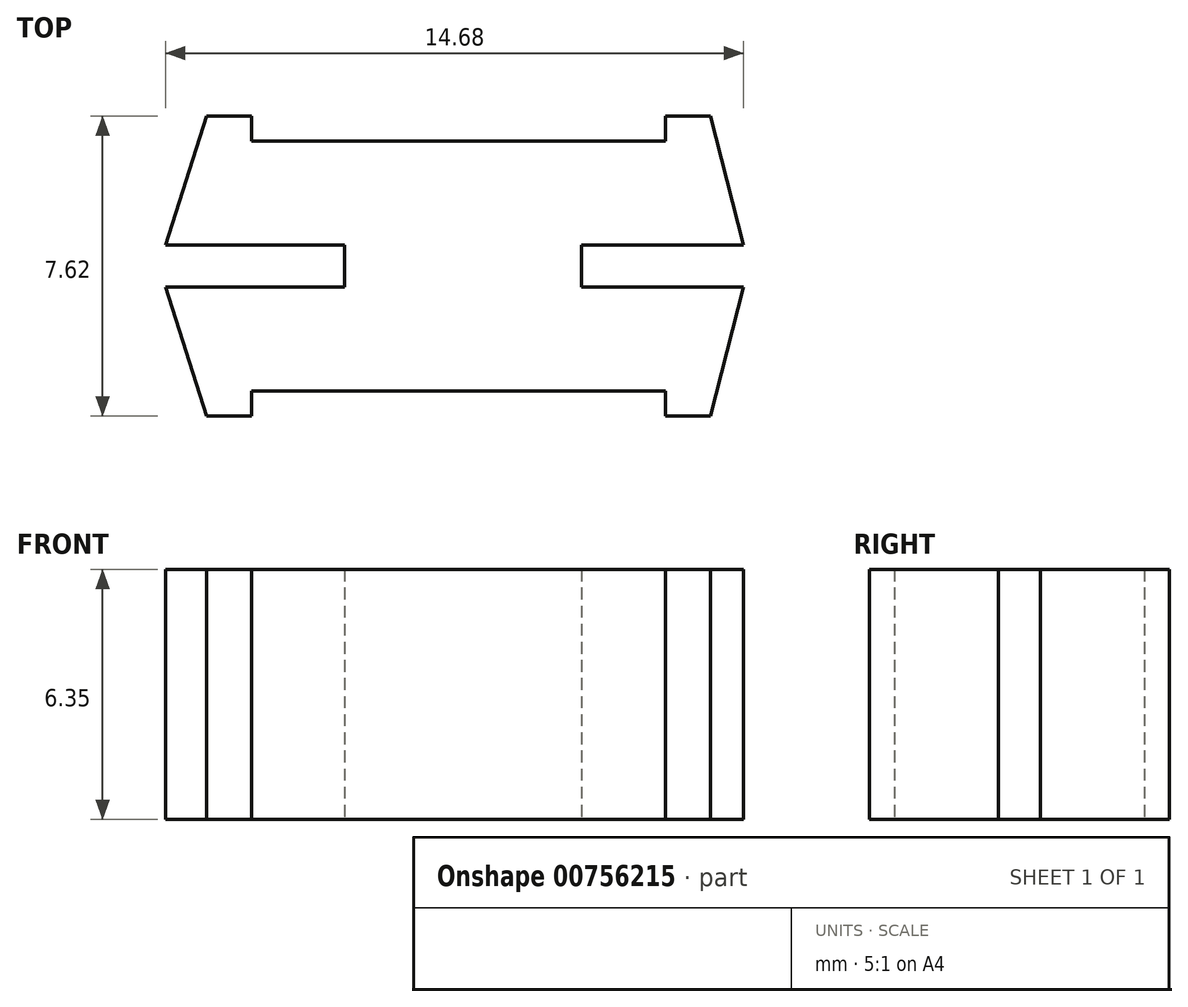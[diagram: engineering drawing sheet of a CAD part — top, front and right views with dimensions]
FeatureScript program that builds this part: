
annotation { "Feature Type Name" : "Feature", "Feature Type Description" : "" }
export const myFeature = defineFeature(function(context is Context, id is Id, definition is map)
    precondition{}
    {
        {
            var Q0;
            Q0=qCreatedBy(makeId("Top.planeOp"),FACE);
            var sketch = newSketch(context, id + "F0", { "sketchPlane" : qUnion([Q0])});
            skLineSegment(sketch, "E0", {"start": v(-7.6, 0) * mm, "end": v(7.38, 0) * mm});
            skLineSegment(sketch, "E1.bottom", {"start": v(-5.25, -3.18) * mm, "end": v(5.25, -3.18) * mm});
            skLineSegment(sketch, "E1.top", {"start": v(-5.25, 3.18) * mm, "end": v(5.25, 3.18) * mm});
            skLineSegment(sketch, "E1.left", {"start": v(-5.25, -3.18) * mm, "end": v(-5.25, 3.18) * mm});
            skLineSegment(sketch, "E1.right", {"start": v(5.25, -3.18) * mm, "end": v(5.25, 3.18) * mm});
            skPoint(sketch, "E1.middle", {"position": v(0, 0) * mm});
            skPoint(sketch, "E2", {"position": v(-5.25, 0) * mm});
            skPoint(sketch, "E3", {"position": v(5.25, 0) * mm});
            skLineSegment(sketch, "E4", {"start": v(-5.25, 0) * mm, "end": v(-5.25, 3.81) * mm});
            skLineSegment(sketch, "E5", {"start": v(-5.25, 0) * mm, "end": v(-5.25, -3.81) * mm});
            skLineSegment(sketch, "E6", {"start": v(5.25, 0) * mm, "end": v(5.25, 3.8) * mm});
            skLineSegment(sketch, "E7", {"start": v(5.25, 0) * mm, "end": v(5.25, -3.81) * mm});
            skLineSegment(sketch, "E8", {"start": v(-5.25, 3.81) * mm, "end": v(-6.4, 3.81) * mm});
            skLineSegment(sketch, "E9", {"start": v(-5.25, -3.81) * mm, "end": v(-6.4, -3.81) * mm});
            skLineSegment(sketch, "E10", {"start": v(5.25, 3.8) * mm, "end": v(6.4, 3.8) * mm});
            skLineSegment(sketch, "E11", {"start": v(5.25, -3.81) * mm, "end": v(6.4, -3.81) * mm});
            skLineSegment(sketch, "E12", {"start": v(-7.6, 0) * mm, "end": v(-6.4, -3.8) * mm});
            skLineSegment(sketch, "E13", {"start": v(-7.6, 0) * mm, "end": v(-6.4, 3.8) * mm});
            skLineSegment(sketch, "E14", {"start": v(6.4, 3.81) * mm, "end": v(7.38, 0) * mm});
            skLineSegment(sketch, "E15", {"start": v(6.4, -3.81) * mm, "end": v(7.38, 0) * mm});
            skPoint(sketch, "E16", {"position": v(-3.91, 0) * mm});
            skPoint(sketch, "E17", {"position": v(3.91, 0) * mm});
            skLineSegment(sketch, "E18.bottom", {"start": v(-7.6, -0.54) * mm, "end": v(-2.9, -0.54) * mm});
            skLineSegment(sketch, "E18.top", {"start": v(-7.6, 0.54) * mm, "end": v(-2.9, 0.54) * mm});
            skLineSegment(sketch, "E18.left", {"start": v(-7.6, -0.54) * mm, "end": v(-7.6, 0.54) * mm});
            skLineSegment(sketch, "E18.right", {"start": v(-2.9, -0.54) * mm, "end": v(-2.9, 0.54) * mm});
            skLineSegment(sketch, "E19.bottom", {"start": v(7.38, -0.53) * mm, "end": v(3.13, -0.53) * mm});
            skLineSegment(sketch, "E19.top", {"start": v(7.38, 0.53) * mm, "end": v(3.13, 0.53) * mm});
            skLineSegment(sketch, "E19.left", {"start": v(7.38, -0.53) * mm, "end": v(7.38, 0.53) * mm});
            skLineSegment(sketch, "E19.right", {"start": v(3.13, -0.53) * mm, "end": v(3.13, 0.53) * mm});
            skPoint(sketch, "E20", {"position": v(0, 3.18) * mm});
            skPoint(sketch, "E21", {"position": v(0, -3.18) * mm});
            skSolve(sketch);
        }
        {
            var Q0;
            {var subQ1=sQuery(id+"F0.wireOp",EDGE,"E1.top");Q0=makeQuery(id+"F0.imprint","IMPRINT",FACE,{"disambiguationData":[TD([[makeQuery(id+"F0.imprint","IMPRINT",EDGE,{"derivedFrom":subQ1}),-1.0]])]});}
            var Q1;
            {var subQ1=sQuery(id+"F0.wireOp",EDGE,"E1.bottom");Q1=makeQuery(id+"F0.imprint","IMPRINT",FACE,{"disambiguationData":[TD([[makeQuery(id+"F0.imprint","IMPRINT",EDGE,{"derivedFrom":subQ1}),1.0]])]});}
            var Q2;
            {var subQ1=sQuery(id+"F0.wireOp",EDGE,"E11");Q2=makeQuery(id+"F0.imprint","IMPRINT",FACE,{"disambiguationData":[TD([[makeQuery(id+"F0.imprint","IMPRINT",EDGE,{"derivedFrom":subQ1}),1.0]])]});}
            var Q3;
            {var subQ1=sQuery(id+"F0.wireOp",EDGE,"E10");Q3=makeQuery(id+"F0.imprint","IMPRINT",FACE,{"disambiguationData":[TD([[makeQuery(id+"F0.imprint","IMPRINT",EDGE,{"derivedFrom":subQ1}),-1.0]])]});}
            var Q4;
            {var subQ1=sQuery(id+"F0.wireOp",EDGE,"E8");Q4=makeQuery(id+"F0.imprint","IMPRINT",FACE,{"disambiguationData":[TD([[makeQuery(id+"F0.imprint","IMPRINT",EDGE,{"derivedFrom":subQ1}),1.0]])]});}
            var Q5;
            {var subQ1=sQuery(id+"F0.wireOp",EDGE,"E9");Q5=makeQuery(id+"F0.imprint","IMPRINT",FACE,{"disambiguationData":[TD([[makeQuery(id+"F0.imprint","IMPRINT",EDGE,{"derivedFrom":subQ1}),-1.0]])]});}
            extrude(context, id + "F1", {"entities" : qUnion([Q0, Q1, Q2, Q3, Q4, Q5]), "depth" : 6.35 * mm, "offsetDistance" : 25.4 * mm});
        }
    });
